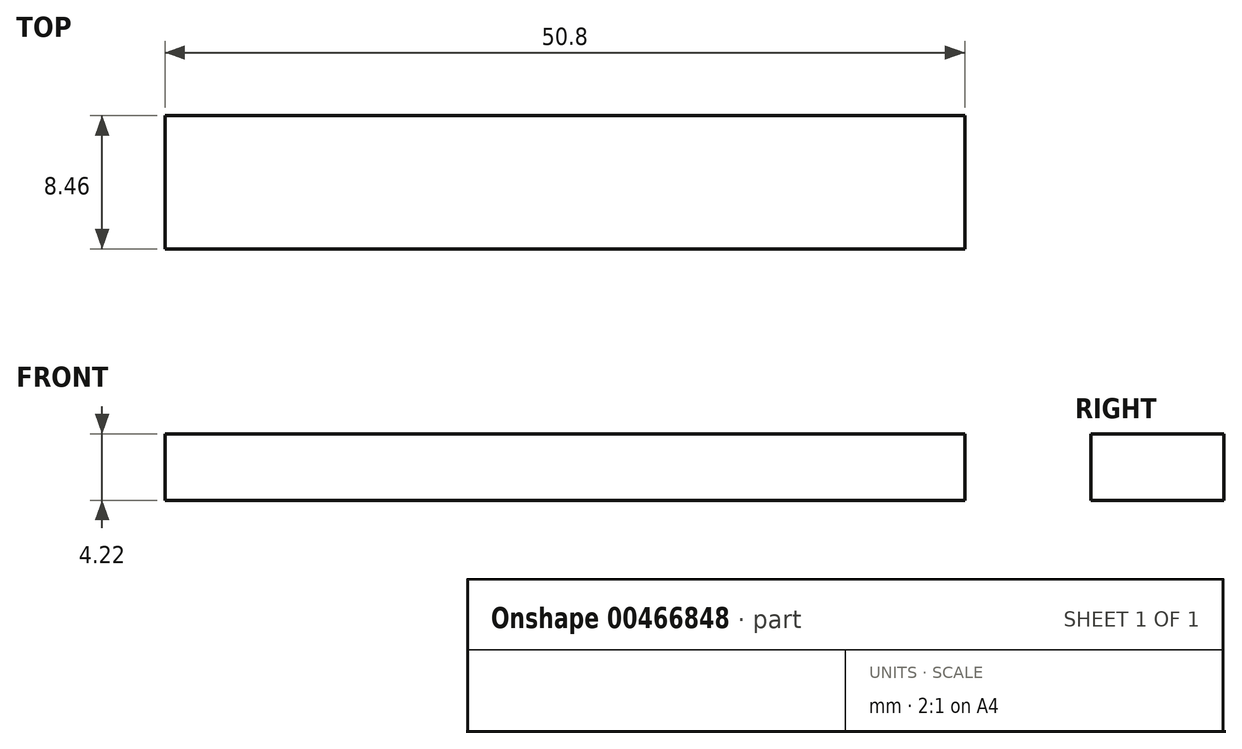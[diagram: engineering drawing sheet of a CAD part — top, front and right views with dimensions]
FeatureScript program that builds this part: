
annotation { "Feature Type Name" : "Feature", "Feature Type Description" : "" }
export const myFeature = defineFeature(function(context is Context, id is Id, definition is map)
    precondition{}
    {
        {
            var Q0;
            Q0=qCreatedBy(makeId("Top.planeOp"),FACE);
            var sketch = newSketch(context, id + "F0", { "sketchPlane" : qUnion([Q0])});
            skLineSegment(sketch, "E0.bottom", {"start": v(-26.09, 12.35) * mm, "end": v(24.71, 12.35) * mm});
            skLineSegment(sketch, "E0.top", {"start": v(-26.09, 3.9) * mm, "end": v(24.71, 3.9) * mm});
            skLineSegment(sketch, "E0.left", {"start": v(-26.09, 12.35) * mm, "end": v(-26.09, 3.9) * mm});
            skLineSegment(sketch, "E0.right", {"start": v(24.71, 12.35) * mm, "end": v(24.71, 3.9) * mm});
            skSolve(sketch);
        }
        {
            var Q0;
            Q0 = qSketchRegion(id + "F0", true);
            extrude(context, id + "F1", {"entities" : qUnion([Q0]), "depth" : 4.22 * mm});
        }
    });
